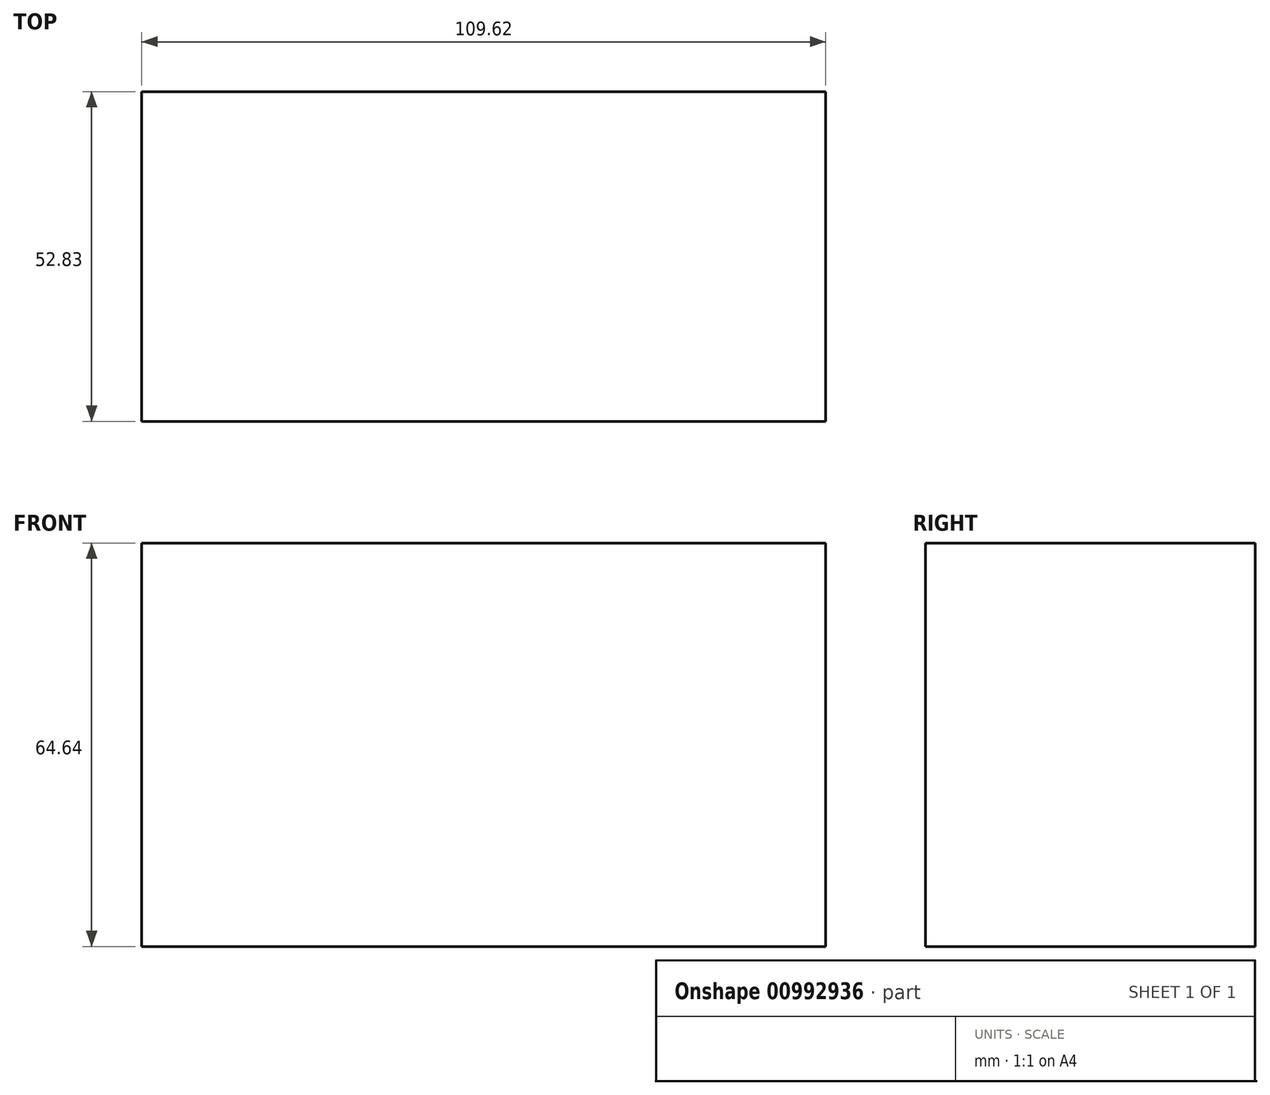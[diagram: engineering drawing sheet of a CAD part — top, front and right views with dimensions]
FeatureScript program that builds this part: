
annotation { "Feature Type Name" : "Feature", "Feature Type Description" : "" }
export const myFeature = defineFeature(function(context is Context, id is Id, definition is map)
    precondition{}
    {
        {
            var Q0;
            Q0=qCreatedBy(makeId("Front.planeOp"),FACE);
            var sketch = newSketch(context, id + "F0", { "sketchPlane" : qUnion([Q0])});
            skLineSegment(sketch, "E0.bottom", {"start": v(54.8, 32.32) * mm, "end": v(-54.8, 32.32) * mm});
            skLineSegment(sketch, "E0.top", {"start": v(54.8, -32.32) * mm, "end": v(-54.8, -32.32) * mm});
            skLineSegment(sketch, "E0.left", {"start": v(54.8, 32.32) * mm, "end": v(54.8, -32.32) * mm});
            skLineSegment(sketch, "E0.right", {"start": v(-54.8, 32.32) * mm, "end": v(-54.8, -32.32) * mm});
            skPoint(sketch, "E0.middle", {"position": v(0, 0) * mm});
            skSolve(sketch);
        }
        {
            var Q0;
            Q0=makeQuery(id+"F0.imprint","IMPRINT",FACE,{"disambiguationData":[TD([[makeQuery(id+"F0.imprint","IMPRINT",EDGE,{"derivedFrom":sQuery(id+"F0.wireOp",EDGE,"E0.bottom")}),1.0]])]});
            extrude(context, id + "F1", {"entities" : qUnion([Q0]), "depth" : 52.83 * mm, "offsetDistance" : 25.4 * mm});
        }
    });
